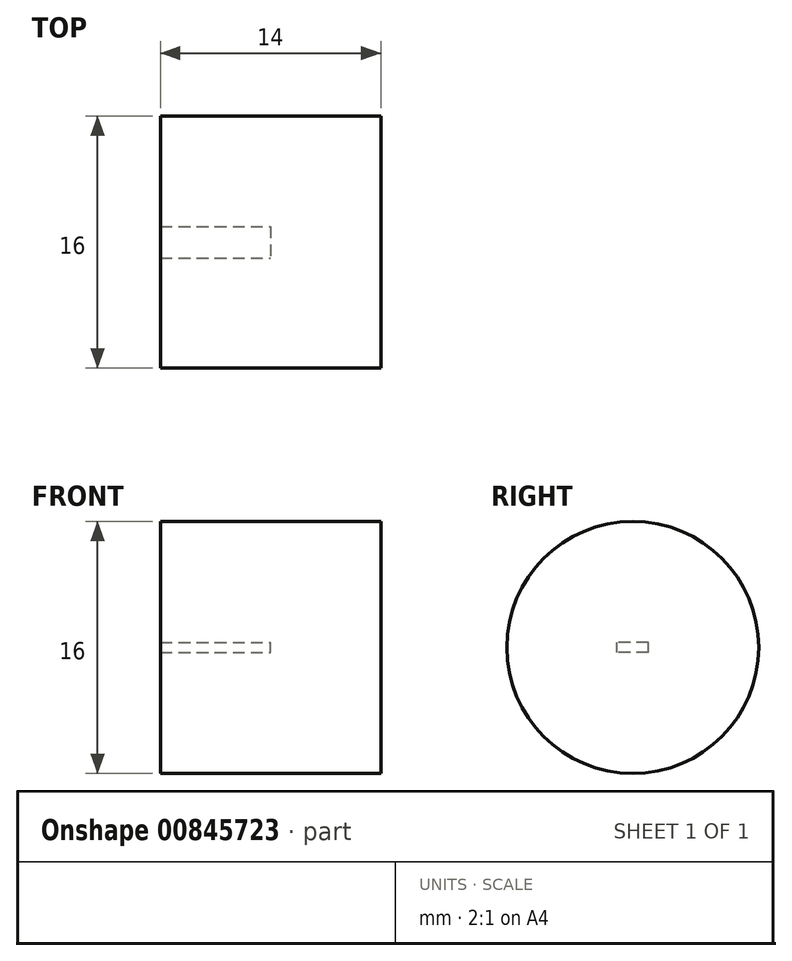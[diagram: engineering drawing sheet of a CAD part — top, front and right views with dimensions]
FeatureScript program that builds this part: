
annotation { "Feature Type Name" : "Feature", "Feature Type Description" : "" }
export const myFeature = defineFeature(function(context is Context, id is Id, definition is map)
    precondition{}
    {
        {
            var Q0;
            Q0=qCreatedBy(makeId("Right.planeOp"),FACE);
            var sketch = newSketch(context, id + "F0", { "sketchPlane" : qUnion([Q0])});
            skCircle(sketch, "E0", {"center": v(0, 0) * mm, "radius": 8 * mm});
            skSolve(sketch);
        }
        {
            var Q0;
            Q0=makeQuery(id+"F0.imprint","IMPRINT",FACE,{"disambiguationData":[TD([[makeQuery(id+"F0.imprint","IMPRINT",EDGE,{"derivedFrom":sQuery(id+"F0.wireOp",EDGE,"E0")}),1.0]])]});
            extrude(context, id + "F1", {"entities" : qUnion([Q0]), "depth" : 14 * mm, "offsetDistance" : 25 * mm});
        }
        {
            var Q0;
            Q0=qCreatedBy(makeId("Right.planeOp"),FACE);
            var sketch = newSketch(context, id + "F2", { "sketchPlane" : qUnion([Q0])});
            skLineSegment(sketch, "E1.bottom", {"start": v(0.32, -0.31) * mm, "end": v(-0.31, -0.31) * mm});
            skLineSegment(sketch, "E1.top", {"start": v(0.32, 0.32) * mm, "end": v(-0.31, 0.32) * mm});
            skLineSegment(sketch, "E1.left", {"start": v(0.32, -0.31) * mm, "end": v(0.32, 0.32) * mm});
            skLineSegment(sketch, "E1.right", {"start": v(-0.31, -0.31) * mm, "end": v(-0.31, 0.32) * mm});
            skPoint(sketch, "E1.middle", {"position": v(0, 0) * mm});
            skSolve(sketch);
        }
        {
            var Q0;
            Q0=makeQuery(id+"F2.imprint","IMPRINT",FACE,{"disambiguationData":[TD([[makeQuery(id+"F2.imprint","IMPRINT",EDGE,{"derivedFrom":sQuery(id+"F2.wireOp",EDGE,"E1.bottom")}),-1.0]])]});
            extrude(context, id + "F3", {"entities" : qUnion([Q0]), "operationType" : NewBodyOperationType.REMOVE, "depth" : 7 * mm, "offsetDistance" : 25 * mm});
        }
        {
            var Q0;
            Q0=qCreatedBy(makeId("Right.planeOp"),FACE);
            var sketch = newSketch(context, id + "F4", { "sketchPlane" : qUnion([Q0])});
            skLineSegment(sketch, "E2.bottom", {"start": v(1, -0.31) * mm, "end": v(-1, -0.32) * mm});
            skLineSegment(sketch, "E2.top", {"start": v(1, 0.32) * mm, "end": v(-1, 0.31) * mm});
            skLineSegment(sketch, "E2.left", {"start": v(1, -0.31) * mm, "end": v(1, 0.32) * mm});
            skLineSegment(sketch, "E2.right", {"start": v(-1, -0.32) * mm, "end": v(-1, 0.31) * mm});
            skPoint(sketch, "E2.middle", {"position": v(0, 0) * mm});
            skSolve(sketch);
        }
        {
            var Q0;
            Q0=makeQuery(id+"F1.opExtrude","CAP_FACE",FACE,{"disambiguationData":[OSD([sQuery(id+"F0.wireOp",EDGE,"E0")])],"isStart":true});
            cPlane(context, id + "F5", {"entities" : qUnion([Q0]), "cplaneType" : CPlaneType.OFFSET, "offset" : 7 * mm, "oppositeDirection" : true, "width" : 150 * mm, "height" : 150 * mm});
        }
        {
            var Q0;
            Q0=qCreatedBy(id+"F5.planeOp",FACE);
            var sketch = newSketch(context, id + "F6", { "sketchPlane" : qUnion([Q0])});
            skLineSegment(sketch, "E3.bottom", {"start": v(-1, -0.32) * mm, "end": v(1, -0.32) * mm});
            skLineSegment(sketch, "E3.top", {"start": v(-1, 0.32) * mm, "end": v(1, 0.32) * mm});
            skLineSegment(sketch, "E3.left", {"start": v(-1, -0.32) * mm, "end": v(-1, 0.31) * mm});
            skLineSegment(sketch, "E3.right", {"start": v(1, -0.32) * mm, "end": v(1, 0.31) * mm});
            skPoint(sketch, "E3.middle", {"position": v(0, 0) * mm});
            skLineSegment(sketch, "E4.0", {"start": v(-0.32, -0.31) * mm, "end": v(-0.32, 0.32) * mm});
            skLineSegment(sketch, "E5.0", {"start": v(0.31, -0.31) * mm, "end": v(0.31, 0.32) * mm});
            skPoint(sketch, "E6.0", {"position": v(0.31, 0) * mm});
            skPoint(sketch, "E7.0", {"position": v(-0.32, 0) * mm});
            skLineSegment(sketch, "E8.0", {"start": v(-1, 0.32) * mm, "end": v(1, 0.31) * mm});
            skSolve(sketch);
        }
        {
            var Q0;
            Q0 = qSketchRegion(id + "F6", true);
            extrude(context, id + "F7", {"entities" : qUnion([Q0]), "operationType" : NewBodyOperationType.REMOVE, "depth" : 7 * mm, "offsetDistance" : 25 * mm});
        }
    });
